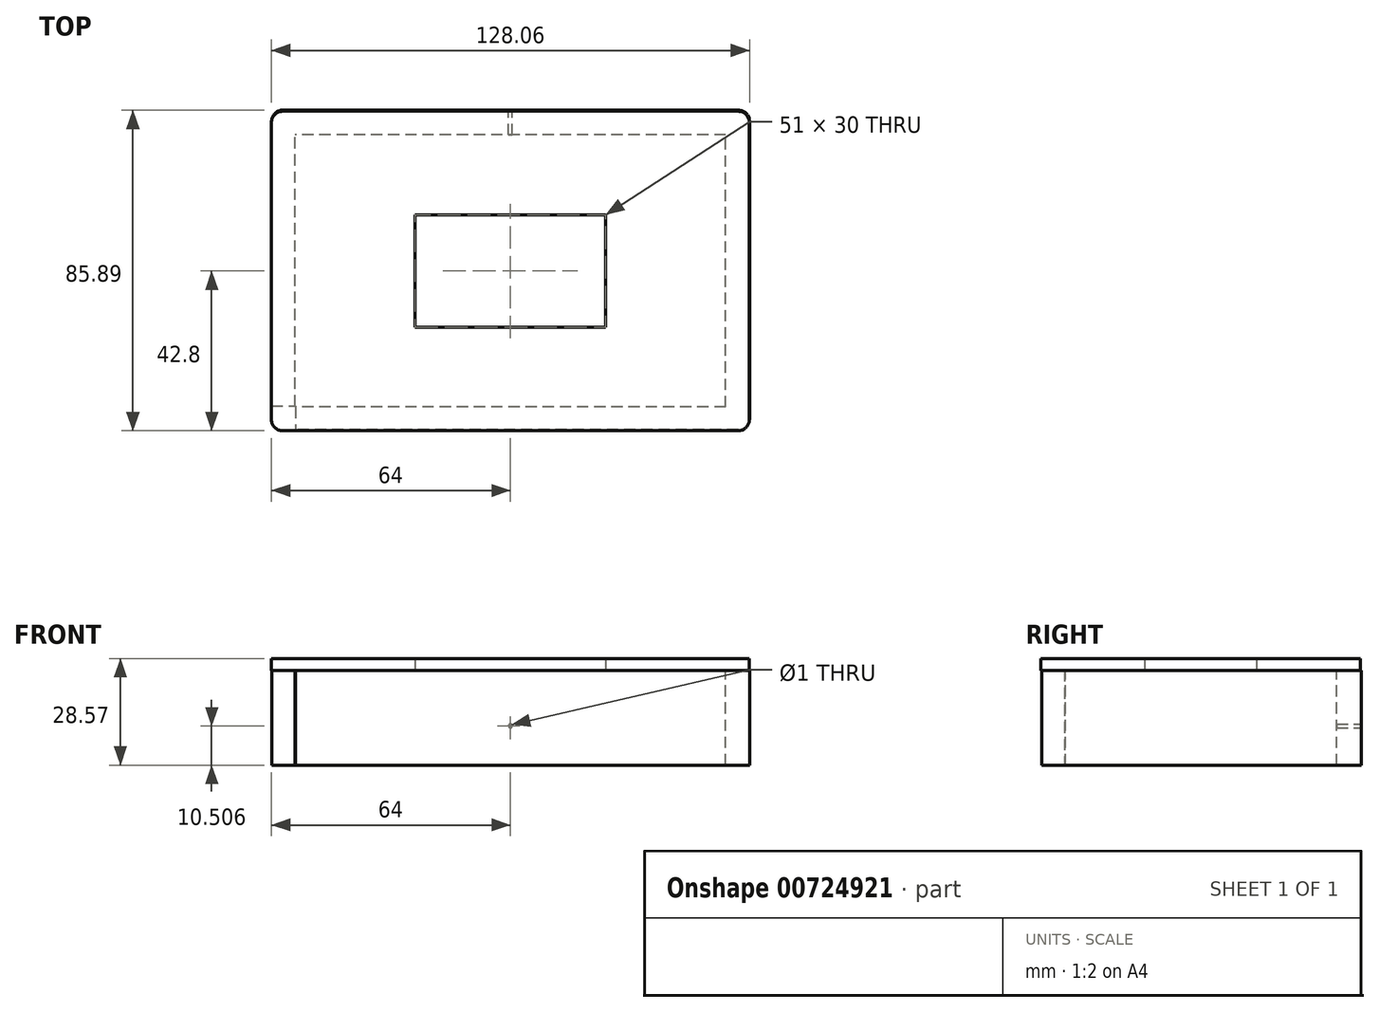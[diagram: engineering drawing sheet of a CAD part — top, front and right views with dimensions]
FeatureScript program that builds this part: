
annotation { "Feature Type Name" : "Feature", "Feature Type Description" : "" }
export const myFeature = defineFeature(function(context is Context, id is Id, definition is map)
    precondition{}
    {
        {
            var Q0;
            Q0=qCreatedBy(makeId("Top.planeOp"),FACE);
            var sketch = newSketch(context, id + "F0", { "sketchPlane" : qUnion([Q0])});
            skLineSegment(sketch, "E0.bottom", {"start": v(-61, 42.8) * mm, "end": v(61, 42.8) * mm});
            skLineSegment(sketch, "E0.top", {"start": v(-61, -42.8) * mm, "end": v(61, -42.8) * mm});
            skLineSegment(sketch, "E0.left", {"start": v(-64, 39.8) * mm, "end": v(-64, -39.8) * mm});
            skLineSegment(sketch, "E0.right", {"start": v(64, 39.8) * mm, "end": v(64, -39.8) * mm});
            skPoint(sketch, "E0.middle", {"position": v(0, 0) * mm});
            skPoint(sketch, "E1.visualSharp", {"position": v(-64, 42.8) * mm});
            skArc(sketch, "E1.filletArc", {"start": v(-61, 42.8) * mm, "mid": v(-63.12, 41.92) * mm, "end": v(-64, 39.8) * mm});
            skPoint(sketch, "E2.visualSharp", {"position": v(-64, -42.8) * mm});
            skArc(sketch, "E2.filletArc", {"start": v(-64, -39.8) * mm, "mid": v(-63.12, -41.92) * mm, "end": v(-61, -42.8) * mm});
            skPoint(sketch, "E3.visualSharp", {"position": v(64, 42.8) * mm});
            skArc(sketch, "E3.filletArc", {"start": v(64, 39.8) * mm, "mid": v(63.12, 41.92) * mm, "end": v(61, 42.8) * mm});
            skPoint(sketch, "E4.visualSharp", {"position": v(64, -42.8) * mm});
            skArc(sketch, "E4.filletArc", {"start": v(61, -42.8) * mm, "mid": v(63.12, -41.92) * mm, "end": v(64, -39.8) * mm});
            skLineSegment(sketch, "E5.bottom", {"start": v(25.5, -15) * mm, "end": v(-25.5, -15) * mm});
            skLineSegment(sketch, "E5.top", {"start": v(25.5, 15) * mm, "end": v(-25.5, 15) * mm});
            skLineSegment(sketch, "E5.left", {"start": v(25.5, -15) * mm, "end": v(25.5, 15) * mm});
            skLineSegment(sketch, "E5.right", {"start": v(-25.5, -15) * mm, "end": v(-25.5, 15) * mm});
            skSolve(sketch);
        }
        {
            var Q0;
            Q0 = qSketchRegion(id + "F0", true);
            extrude(context, id + "F1", {"entities" : qUnion([Q0]), "depth" : 3.17 * mm, "offsetDistance" : 25 * mm});
        }
        {
            var Q0;
            Q0=qCreatedBy(makeId("Top.planeOp"),FACE);
            var sketch = newSketch(context, id + "F2", { "sketchPlane" : qUnion([Q0])});
            skLineSegment(sketch, "E6.bottom", {"start": v(57.71, -36.16) * mm, "end": v(-57.59, -36.16) * mm});
            skLineSegment(sketch, "E6.top", {"start": v(61.06, -42.5) * mm, "end": v(-57.59, -42.5) * mm});
            skLineSegment(sketch, "E6.left", {"start": v(64.06, -36.16) * mm, "end": v(64.06, -39.5) * mm});
            skLineSegment(sketch, "E6.right", {"start": v(-57.59, -36.16) * mm, "end": v(-57.59, -42.5) * mm});
            skPoint(sketch, "E7.visualSharp", {"position": v(64.06, -42.5) * mm});
            skArc(sketch, "E7.filletArc", {"start": v(61.06, -42.5) * mm, "mid": v(63.18, -41.63) * mm, "end": v(64.06, -39.5) * mm});
            skLineSegment(sketch, "E8.bottom", {"start": v(-60.94, 43.1) * mm, "end": v(-57.59, 43.1) * mm});
            skLineSegment(sketch, "E8.top", {"start": v(-63.94, -36.16) * mm, "end": v(-57.59, -36.16) * mm});
            skLineSegment(sketch, "E8.left", {"start": v(-63.94, 40.1) * mm, "end": v(-63.94, -36.16) * mm});
            skLineSegment(sketch, "E8.right", {"start": v(-57.59, 36.74) * mm, "end": v(-57.59, -36.16) * mm});
            skPoint(sketch, "E9.visualSharp", {"position": v(-63.94, 43.1) * mm});
            skArc(sketch, "E9.filletArc", {"start": v(-60.94, 43.1) * mm, "mid": v(-63.06, 42.22) * mm, "end": v(-63.94, 40.1) * mm});
            skLineSegment(sketch, "E10.bottom", {"start": v(-57.59, 43.1) * mm, "end": v(61.06, 43.1) * mm});
            skLineSegment(sketch, "E10.top", {"start": v(-57.59, 36.74) * mm, "end": v(57.71, 36.74) * mm});
            skLineSegment(sketch, "E10.right", {"start": v(64.06, 40.1) * mm, "end": v(64.06, 36.74) * mm});
            skPoint(sketch, "E11.visualSharp", {"position": v(64.06, 43.1) * mm});
            skArc(sketch, "E11.filletArc", {"start": v(64.06, 40.1) * mm, "mid": v(63.18, 42.22) * mm, "end": v(61.06, 43.1) * mm});
            skLineSegment(sketch, "E12.left", {"start": v(64.06, 36.74) * mm, "end": v(64.06, -36.16) * mm});
            skLineSegment(sketch, "E12.right", {"start": v(57.71, 36.74) * mm, "end": v(57.71, -36.16) * mm});
            skSolve(sketch);
        }
        {
            var Q0;
            Q0=qCreatedBy(makeId("Top.planeOp"),FACE);
            var sketch = newSketch(context, id + "F3", { "sketchPlane" : qUnion([Q0])});
            skLineSegment(sketch, "E13.bottom", {"start": v(57.65, -36.45) * mm, "end": v(-57.65, -36.45) * mm});
            skLineSegment(sketch, "E13.top", {"start": v(57.65, 36.45) * mm, "end": v(-57.65, 36.45) * mm});
            skLineSegment(sketch, "E13.left", {"start": v(57.65, -36.45) * mm, "end": v(57.65, 36.45) * mm});
            skLineSegment(sketch, "E13.right", {"start": v(-57.65, -36.45) * mm, "end": v(-57.65, 36.45) * mm});
            skPoint(sketch, "E13.middle", {"position": v(0, 0) * mm});
            skSolve(sketch);
        }
        {
            var Q0;
            Q0 = qSketchRegion(id + "F2", true);
            extrude(context, id + "F4", {"entities" : qUnion([Q0]), "operationType" : NewBodyOperationType.ADD, "oppositeDirection" : true, "depth" : 25.4 * mm, "offsetDistance" : 25 * mm});
        }
        {
            var Q0;
            Q0 = qSketchRegion(id + "F3", true);
            extrude(context, id + "F5", {"entities" : qUnion([Q0]), "operationType" : NewBodyOperationType.REMOVE, "oppositeDirection" : true, "depth" : 25.4 * mm, "offsetDistance" : 25 * mm});
        }
        {
            var Q0;
            Q0=makeQuery(id+"F4.opExtrude","SWEPT_FACE",FACE,{"disambiguationData":[OSD([sQuery(id+"F2.wireOp",EDGE,"E8.bottom"),sQuery(id+"F2.wireOp",EDGE,"E10.bottom")])]});
            var sketch = newSketch(context, id + "F6", { "sketchPlane" : qUnion([Q0])});
            skCircle(sketch, "E14", {"center": v(0, -14.9) * mm, "radius": 0.5 * mm});
            skSolve(sketch);
        }
        {
            var Q0;
            Q0 = qSketchRegion(id + "F6", true);
            extrude(context, id + "F7", {"entities" : qUnion([Q0]), "operationType" : NewBodyOperationType.REMOVE, "oppositeDirection" : true, "depth" : 25 * mm, "offsetDistance" : 25 * mm});
        }
    });
